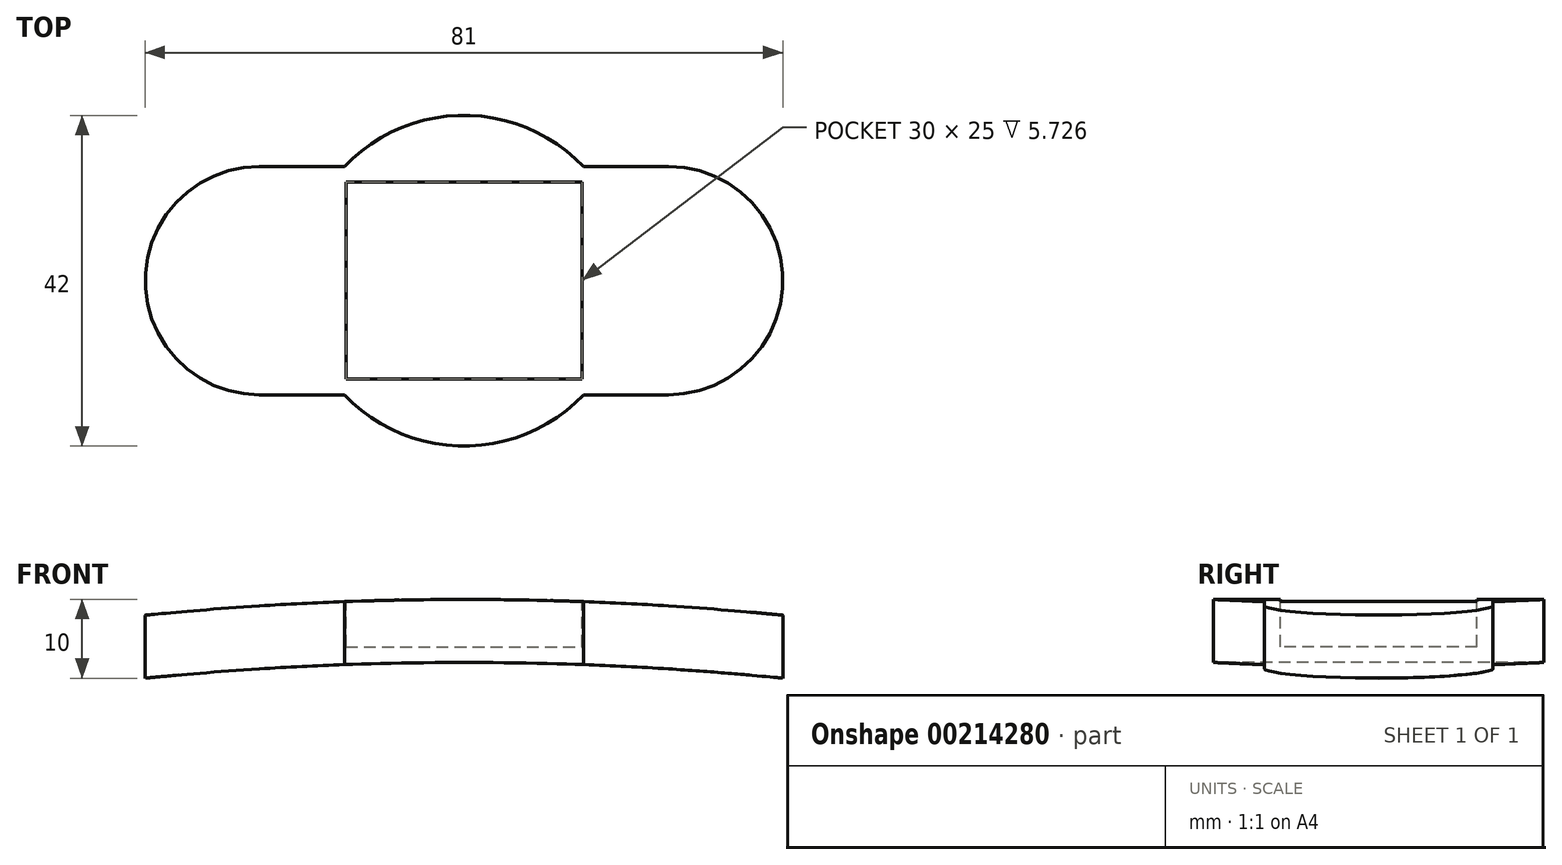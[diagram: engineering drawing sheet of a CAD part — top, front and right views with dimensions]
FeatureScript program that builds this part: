
annotation { "Feature Type Name" : "Feature", "Feature Type Description" : "" }
export const myFeature = defineFeature(function(context is Context, id is Id, definition is map)
    precondition{}
    {
        {
            var Q0;
            Q0=qCreatedBy(makeId("Top.planeOp"),FACE);
            var sketch = newSketch(context, id + "F0", { "sketchPlane" : qUnion([Q0])});
            skCircle(sketch, "E0", {"center": v(0, 0) * mm, "radius": 21 * mm});
            skCircle(sketch, "E1", {"center": v(-26, 0) * mm, "radius": 14.5 * mm});
            skLineSegment(sketch, "E2", {"start": v(0, 21) * mm, "end": v(0, -21) * mm, "construction": true});
            skLineSegment(sketch, "E3", {"start": v(-26, 14.5) * mm, "end": v(-15.2, 14.5) * mm});
            skLineSegment(sketch, "E4", {"start": v(-26, 43.47) * mm, "end": v(-26, -46.78) * mm, "construction": true});
            skLineSegment(sketch, "E5", {"start": v(-26, -14.5) * mm, "end": v(-15.2, -14.5) * mm});
            skLineSegment(sketch, "E6.MirrorCS", {"start": v(26, -14.5) * mm, "end": v(15.2, -14.5) * mm});
            skCircle(sketch, "E7.MirrorC", {"center": v(26, 0) * mm, "radius": 14.5 * mm});
            skLineSegment(sketch, "E8.MirrorCS", {"start": v(26, 14.5) * mm, "end": v(15.2, 14.5) * mm});
            skLineSegment(sketch, "E9", {"start": v(-40.5, 19) * mm, "end": v(-40.5, -20.14) * mm, "construction": true});
            skSolve(sketch);
        }
        {
            var Q0;
            Q0 = qSketchRegion(id + "F0", true);
            var Q1;
            {var subQ0=sQuery(id+"F0.wireOp",EDGE,"E1");var subQ1=sQuery(id+"F0.wireOp",EDGE,"E0");var subQ2=makeQuery(id+"F0.imprint","INTERSECT",VERTEX,{"disambiguationData":[OD(0.0)],"derivedFrom":[subQ1,subQ0]});Q1=makeQuery(id+"F0.imprint","IMPRINT",FACE,{"disambiguationData":[TD([[makeQuery(id+"F0.imprint","IMPRINT",EDGE,{"disambiguationData":[TD([[subQ2,-1.0]])],"derivedFrom":subQ1}),1.0]])]});}
            var Q2;
            {var subQ0=sQuery(id+"F0.wireOp",EDGE,"E7.MirrorC");var subQ1=sQuery(id+"F0.wireOp",EDGE,"E0");var subQ2=makeQuery(id+"F0.imprint","INTERSECT",VERTEX,{"disambiguationData":[OD(0.0)],"derivedFrom":[subQ1,subQ0]});Q2=makeQuery(id+"F0.imprint","IMPRINT",FACE,{"disambiguationData":[TD([[makeQuery(id+"F0.imprint","IMPRINT",EDGE,{"disambiguationData":[TD([[subQ2,1.0]])],"derivedFrom":subQ1}),1.0]])]});}
            extrude(context, id + "F1", {"entities" : qUnion([Q0, Q1, Q2]), "depth" : 10 * mm});
        }
        {
            var Q0;
            Q0=makeQuery(id+"F1.opExtrude","CAP_FACE",FACE,{"disambiguationData":[OSD([sQuery(id+"F0.wireOp",EDGE,"E0"),sQuery(id+"F0.wireOp",EDGE,"E1"),sQuery(id+"F0.wireOp",EDGE,"E3"),sQuery(id+"F0.wireOp",EDGE,"E5"),sQuery(id+"F0.wireOp",EDGE,"E6.MirrorCS"),sQuery(id+"F0.wireOp",EDGE,"E7.MirrorC"),sQuery(id+"F0.wireOp",EDGE,"E8.MirrorCS")])],"isStart":false});
            var sketch = newSketch(context, id + "F2", { "sketchPlane" : qUnion([Q0])});
            skLineSegment(sketch, "E10.bottom", {"start": v(-15, 12.5) * mm, "end": v(15, 12.5) * mm});
            skLineSegment(sketch, "E10.top", {"start": v(-15, -12.5) * mm, "end": v(15, -12.5) * mm});
            skLineSegment(sketch, "E10.left", {"start": v(-15, 12.5) * mm, "end": v(-15, -12.5) * mm});
            skLineSegment(sketch, "E10.right", {"start": v(15, 12.5) * mm, "end": v(15, -12.5) * mm});
            skLineSegment(sketch, "E11", {"start": v(0, 21) * mm, "end": v(0, -21) * mm, "construction": true});
            skLineSegment(sketch, "E12", {"start": v(-15, 0) * mm, "end": v(15, 0) * mm, "construction": true});
            skLineSegment(sketch, "E13", {"start": v(0, 0) * mm, "end": v(0, 12.5) * mm, "construction": true});
            skSolve(sketch);
        }
        {
            var Q0;
            Q0=qCreatedBy(makeId("Front.planeOp"),FACE);
            var sketch = newSketch(context, id + "F3", { "sketchPlane" : qUnion([Q0])});
            skLineSegment(sketch, "E14", {"start": v(-40.5, 0) * mm, "end": v(40.5, 0) * mm, "construction": true});
            skLineSegment(sketch, "E15", {"start": v(0, 0) * mm, "end": v(0, 2) * mm, "construction": true});
            skCircle(sketch, "E16", {"center": v(0, -409.06) * mm, "radius": 411.06 * mm});
            skSolve(sketch);
        }
        {
            var Q0;
            Q0=makeQuery(id+"F3.imprint","IMPRINT",FACE,{"disambiguationData":[TD([[makeQuery(id+"F3.imprint","IMPRINT",EDGE,{"derivedFrom":sQuery(id+"F3.wireOp",EDGE,"E16")}),1.0]])]});
            extrude(context, id + "F4", {"entities" : qUnion([Q0]), "operationType" : NewBodyOperationType.REMOVE, "endBound" : BoundingType.SYMMETRIC, "oppositeDirection" : true, "depth" : 100 * mm});
        }
        {
            var Q0;
            Q0 = qSketchRegion(id + "F2", true);
            extrude(context, id + "F5", {"entities" : qUnion([Q0]), "operationType" : NewBodyOperationType.REMOVE, "oppositeDirection" : true, "depth" : 6 * mm});
        }
        {
            var Q0;
            Q0=qCreatedBy(makeId("Front.planeOp"),FACE);
            var sketch = newSketch(context, id + "F6", { "sketchPlane" : qUnion([Q0])});
            skLineSegment(sketch, "E17", {"start": v(-40.5, 10) * mm, "end": v(-40.5, 8) * mm, "construction": true});
            skLineSegment(sketch, "E18", {"start": v(-40.5, 10) * mm, "end": v(40.5, 10) * mm, "construction": true});
            skLineSegment(sketch, "E19", {"start": v(40.5, 10) * mm, "end": v(40.5, 8) * mm, "construction": true});
            skLineSegment(sketch, "E20", {"start": v(0, 0) * mm, "end": v(0, 10) * mm, "construction": true});
            skArc(sketch, "E21", {"start": v(40.5, 8) * mm, "mid": v(0, 10) * mm, "end": v(-40.5, 8) * mm});
            skLineSegment(sketch, "E22", {"start": v(-40.5, 8) * mm, "end": v(-40.5, 38) * mm});
            skLineSegment(sketch, "E23", {"start": v(-40.5, 38) * mm, "end": v(40.5, 38) * mm});
            skLineSegment(sketch, "E24", {"start": v(40.5, 8) * mm, "end": v(40.5, 38) * mm});
            skSolve(sketch);
        }
        {
            var Q0;
            Q0=makeQuery(id+"F6.imprint","IMPRINT",FACE,{"disambiguationData":[TD([[makeQuery(id+"F6.imprint","IMPRINT",EDGE,{"derivedFrom":sQuery(id+"F6.wireOp",EDGE,"E21")}),-1.0]])]});
            extrude(context, id + "F7", {"entities" : qUnion([Q0]), "operationType" : NewBodyOperationType.REMOVE, "endBound" : BoundingType.SYMMETRIC, "oppositeDirection" : true, "depth" : 100 * mm});
        }
    });
